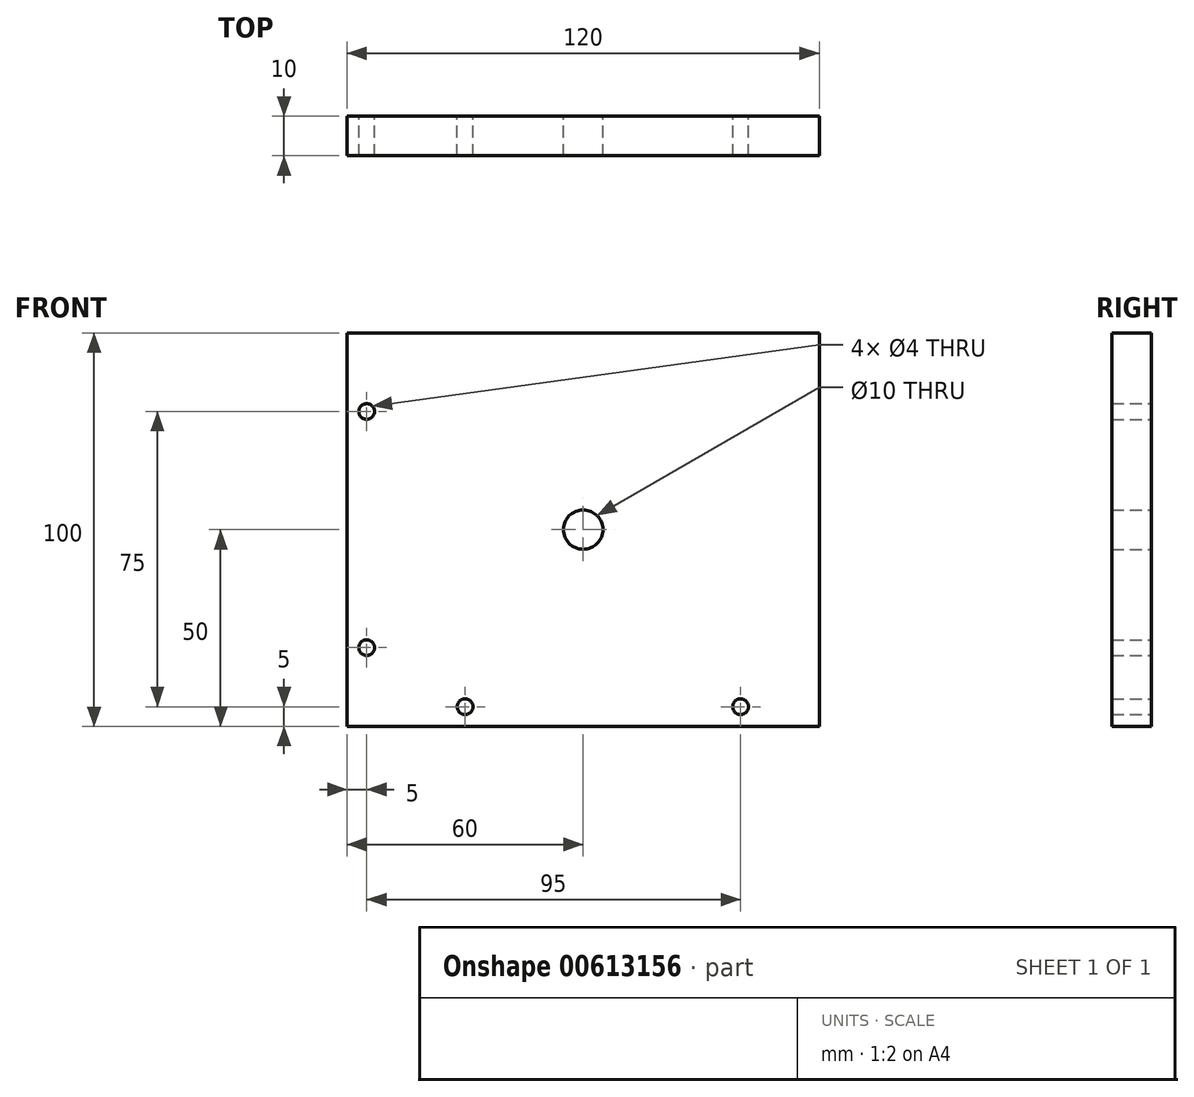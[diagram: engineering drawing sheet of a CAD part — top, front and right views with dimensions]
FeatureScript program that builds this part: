
annotation { "Feature Type Name" : "Feature", "Feature Type Description" : "" }
export const myFeature = defineFeature(function(context is Context, id is Id, definition is map)
    precondition{}
    {
        {
            var Q0;
            Q0=qCreatedBy(makeId("Front.planeOp"),FACE);
            var sketch = newSketch(context, id + "F0", { "sketchPlane" : qUnion([Q0])});
            skLineSegment(sketch, "E0.bottom", {"start": v(60, 50) * mm, "end": v(-60, 50) * mm});
            skLineSegment(sketch, "E0.top", {"start": v(60, -50) * mm, "end": v(-60, -50) * mm});
            skLineSegment(sketch, "E0.left", {"start": v(60, 50) * mm, "end": v(60, -50) * mm});
            skLineSegment(sketch, "E0.right", {"start": v(-60, 50) * mm, "end": v(-60, -50) * mm});
            skPoint(sketch, "E0.middle", {"position": v(0, 0) * mm});
            skCircle(sketch, "E1", {"center": v(0, 0) * mm, "radius": 5 * mm});
            skCircle(sketch, "E2", {"center": v(-30, -45) * mm, "radius": 2 * mm});
            skCircle(sketch, "E3", {"center": v(40, -45) * mm, "radius": 2 * mm});
            skCircle(sketch, "E4", {"center": v(-55, 30) * mm, "radius": 2 * mm});
            skCircle(sketch, "E5", {"center": v(-55, -30) * mm, "radius": 2 * mm});
            skSolve(sketch);
        }
        {
            var Q0;
            Q0=makeQuery(id+"F0.imprint","IMPRINT",FACE,{"disambiguationData":[TD([[makeQuery(id+"F0.imprint","IMPRINT",EDGE,{"derivedFrom":sQuery(id+"F0.wireOp",EDGE,"E0.bottom")}),1.0]])]});
            extrude(context, id + "F1", {"entities" : qUnion([Q0]), "depth" : 10 * mm, "offsetDistance" : 25 * mm});
        }
    });
